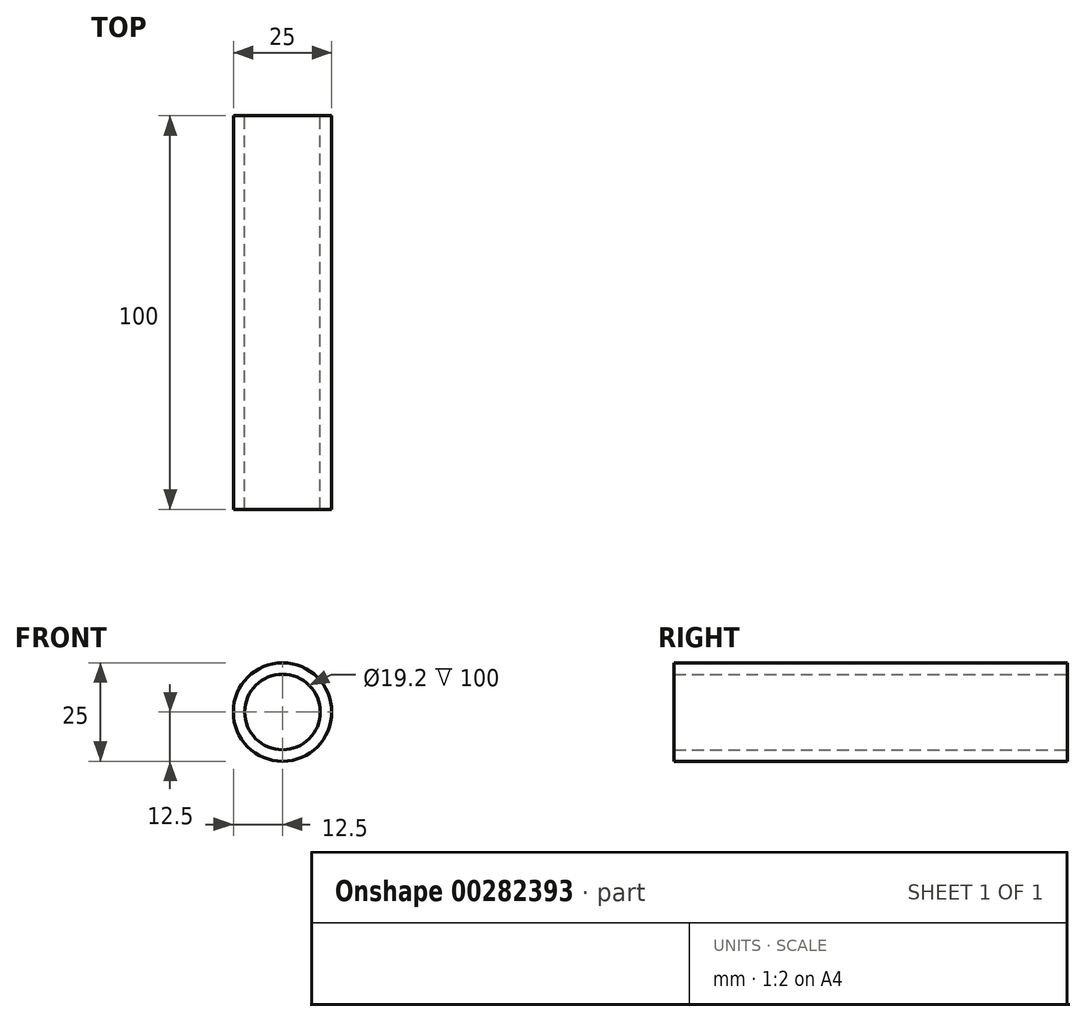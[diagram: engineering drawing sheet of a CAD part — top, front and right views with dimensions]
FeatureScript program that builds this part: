
annotation { "Feature Type Name" : "Feature", "Feature Type Description" : "" }
export const myFeature = defineFeature(function(context is Context, id is Id, definition is map)
    precondition{}
    {
        {
            var Q0;
            Q0=qCreatedBy(makeId("Front.planeOp"),FACE);
            var sketch = newSketch(context, id + "F0", { "sketchPlane" : qUnion([Q0])});
            skCircle(sketch, "E0", {"center": v(0, 0) * mm, "radius": 9.6 * mm});
            skCircle(sketch, "E1", {"center": v(0, 0) * mm, "radius": 12.5 * mm});
            skSolve(sketch);
        }
        {
            var Q0;
            Q0=qSketchRegion(id+"F0",true);
            extrude(context, id + "F1", {"entities" : qUnion([Q0]), "depth" : 100 * mm});
        }
    });
